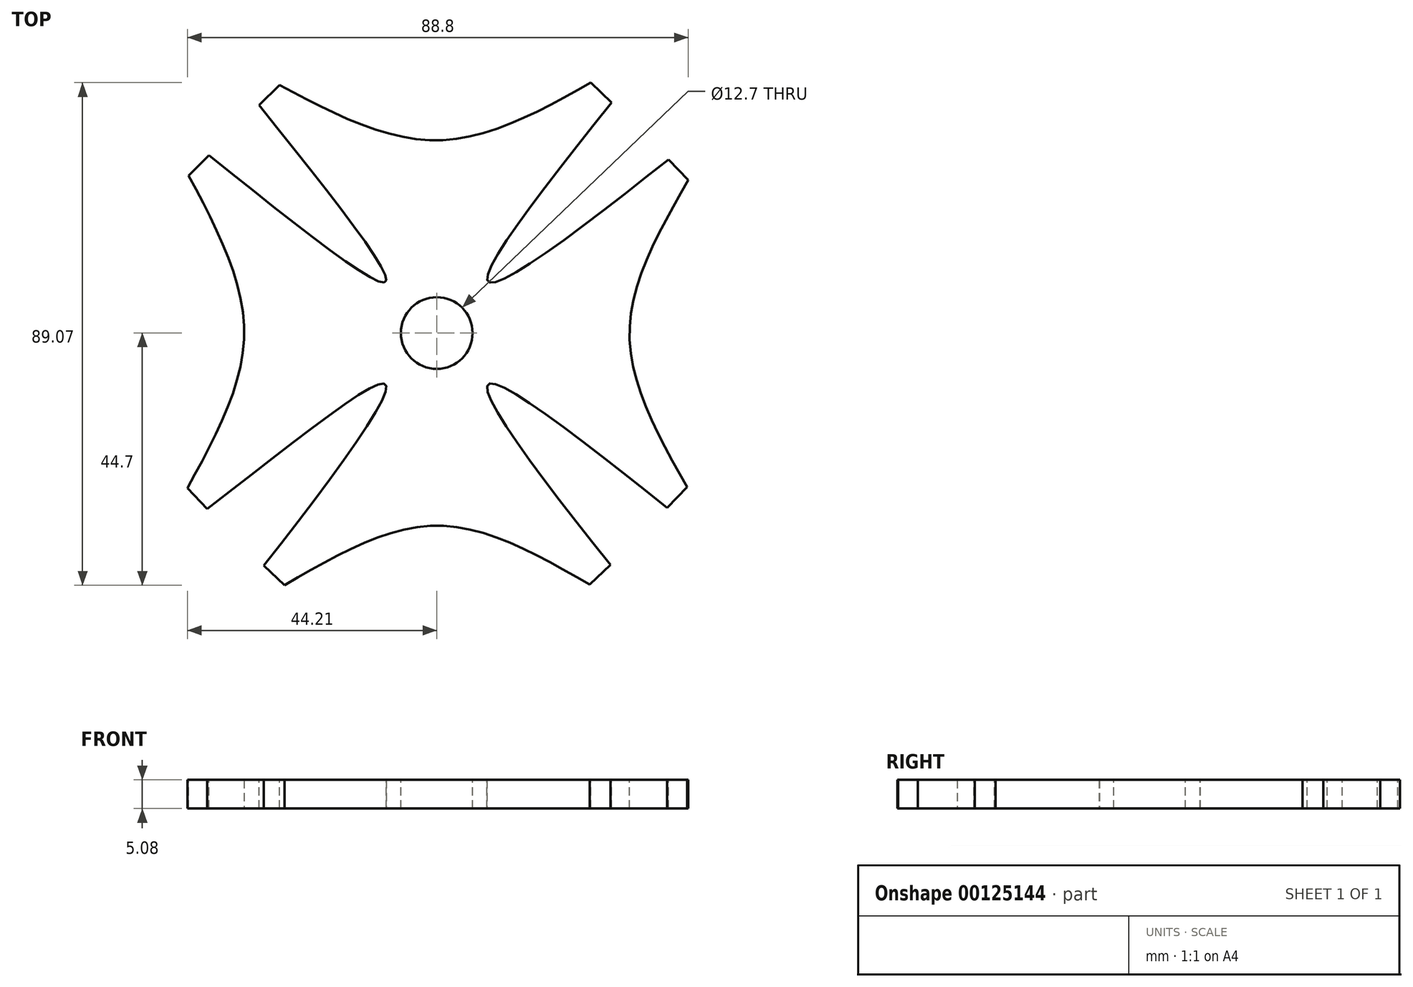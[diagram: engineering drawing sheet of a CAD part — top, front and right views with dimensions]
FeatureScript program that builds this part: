
annotation { "Feature Type Name" : "Feature", "Feature Type Description" : "" }
export const myFeature = defineFeature(function(context is Context, id is Id, definition is map)
    precondition{}
    {
        {
            var Q0;
            Q0=qCreatedBy(makeId("Top.planeOp"),FACE);
            var sketch = newSketch(context, id + "F0", { "sketchPlane" : qUnion([Q0])});
            skCircle(sketch, "E0", {"center": v(0, 0) * mm, "radius": 6.35 * mm});
            skPoint(sketch, "E1", {"position": v(0, -6.35) * mm});
            skPoint(sketch, "E2", {"position": v(6.35, 0) * mm});
            skPoint(sketch, "E3", {"position": v(0, 6.35) * mm});
            skPoint(sketch, "E4", {"position": v(-6.35, 0) * mm});
            skLineSegment(sketch, "E5", {"start": v(0, 6.35) * mm, "end": v(0, 50.8) * mm});
            skLineSegment(sketch, "E6", {"start": v(0, -6.35) * mm, "end": v(0, -50.8) * mm});
            skLineSegment(sketch, "E7", {"start": v(-6.35, 0) * mm, "end": v(-50.8, 0) * mm});
            skLineSegment(sketch, "E8", {"start": v(6.35, 0) * mm, "end": v(50.8, 0) * mm});
            skSolve(sketch);
        }
        {
            var Q0;
            Q0=qCreatedBy(makeId("Top.planeOp"),FACE);
            var sketch = newSketch(context, id + "F1", { "sketchPlane" : qUnion([Q0])});
            skFitSpline(sketch, "E9", {"points": [v(-40.38, 31.49) * mm, v(-9.1, 9.1) * mm, v(-31.49, 40.38) * mm], "startDerivative": vector(89.8, -71.84) * mm, "endDerivative": vector(-71.84, 89.8) * mm});
            skFitSpline(sketch, "E10", {"points": [v(31, 40.86) * mm, v(9.1, 9.1) * mm, v(41.08, 30.77) * mm], "startDerivative": vector(-71.84, -89.8) * mm, "endDerivative": vector(89.8, 71.84) * mm});
            skFitSpline(sketch, "E11", {"points": [v(30.77, -41.08) * mm, v(9.1, -9.1) * mm, v(40.86, -31) * mm], "startDerivative": vector(-71.84, 89.8) * mm, "endDerivative": vector(89.8, -71.84) * mm});
            skLineSegment(sketch, "E12", {"start": v(31, 40.86) * mm, "end": v(27.33, 44.37) * mm});
            skLineSegment(sketch, "E13", {"start": v(41.08, 30.77) * mm, "end": v(44.6, 27.1) * mm});
            skLineSegment(sketch, "E14", {"start": v(40.86, -31) * mm, "end": v(44.37, -27.33) * mm});
            skLineSegment(sketch, "E15", {"start": v(30.77, -41.08) * mm, "end": v(27.1, -44.6) * mm});
            skLineSegment(sketch, "E16", {"start": v(-30.65, -41.19) * mm, "end": v(-26.98, -44.7) * mm});
            skLineSegment(sketch, "E17", {"start": v(-40.69, -31.16) * mm, "end": v(-44.2, -27.5) * mm});
            skLineSegment(sketch, "E18", {"start": v(-40.38, 31.49) * mm, "end": v(-43.97, 27.9) * mm});
            skLineSegment(sketch, "E19", {"start": v(-31.49, 40.38) * mm, "end": v(-27.9, 43.97) * mm});
            skPoint(sketch, "E20", {"position": v(-34.13, 0) * mm});
            skPoint(sketch, "E21", {"position": v(34.17, 0) * mm});
            skFitSpline(sketch, "E22", {"points": [v(-43.97, 27.9) * mm, v(-34.13, 0) * mm, v(-44.2, -27.5) * mm], "startDerivative": vector(29.62, -55.78) * mm, "endDerivative": vector(-30.14, -55) * mm});
            skPoint(sketch, "E23", {"position": v(0, 34.16) * mm});
            skPoint(sketch, "E24", {"position": v(0, -34.14) * mm});
            skFitSpline(sketch, "E25", {"points": [v(-27.9, 43.97) * mm, v(0, 34.16) * mm, v(27.33, 44.37) * mm], "startDerivative": vector(55.8, -29.6) * mm, "endDerivative": vector(54.65, 30.47) * mm});
            skFitSpline(sketch, "E26", {"points": [v(44.6, 27.1) * mm, v(34.17, 0) * mm, v(44.37, -27.33) * mm], "startDerivative": vector(-31.16, -54.18) * mm, "endDerivative": vector(30.7, -54.67) * mm});
            skFitSpline(sketch, "E27", {"points": [v(-26.98, -44.7) * mm, v(0, -34.14) * mm, v(27.1, -44.6) * mm], "startDerivative": vector(53.95, 31.63) * mm, "endDerivative": vector(54.2, -31.4) * mm});
            skFitSpline(sketch, "E28", {"points": [v(-40.69, -31.16) * mm, v(-9.1, -9.1) * mm, v(-30.65, -41.19) * mm], "startDerivative": vector(91.11, 69.9) * mm, "endDerivative": vector(-71.08, -90) * mm});
            skSolve(sketch);
        }
        {
            var Q0;
            Q0=makeQuery(id+"F1.imprint","IMPRINT",FACE,{"disambiguationData":[TD([[makeQuery(id+"F1.imprint","IMPRINT",EDGE,{"derivedFrom":sQuery(id+"F1.wireOp",EDGE,"E9")}),-1.0]])]});
            extrude(context, id + "F2", {"entities" : qUnion([Q0]), "oppositeDirection" : true, "depth" : 5.08 * mm});
        }
        {
            var Q0;
            {var subQ0=sQuery(id+"F0.wireOp",EDGE,"E0");var subQ1=makeQuery(id+"F0.imprint","IMPRINT",VERTEX,{"disambiguationData":[OD(0.0)],"derivedFrom":subQ0});Q0=makeQuery(id+"F0.imprint","IMPRINT",FACE,{"disambiguationData":[TD([[makeQuery(id+"F0.imprint","IMPRINT",EDGE,{"disambiguationData":[TD([[subQ1,1.0]])],"derivedFrom":subQ0}),1.0]])]});}
            var Q1;
            Q1=makeQuery(id+"F2.opExtrude","CAP_FACE",FACE,{"disambiguationData":[OSD([sQuery(id+"F1.wireOp",EDGE,"E9"),sQuery(id+"F1.wireOp",EDGE,"E10"),sQuery(id+"F1.wireOp",EDGE,"E11"),sQuery(id+"F1.wireOp",EDGE,"E12"),sQuery(id+"F1.wireOp",EDGE,"E13"),sQuery(id+"F1.wireOp",EDGE,"E14"),sQuery(id+"F1.wireOp",EDGE,"E15"),sQuery(id+"F1.wireOp",EDGE,"E16"),sQuery(id+"F1.wireOp",EDGE,"E17"),sQuery(id+"F1.wireOp",EDGE,"E18"),sQuery(id+"F1.wireOp",EDGE,"E19"),sQuery(id+"F1.wireOp",EDGE,"E22"),sQuery(id+"F1.wireOp",EDGE,"E25"),sQuery(id+"F1.wireOp",EDGE,"E26"),sQuery(id+"F1.wireOp",EDGE,"E27"),sQuery(id+"F1.wireOp",EDGE,"E28")])],"isStart":false});
            extrude(context, id + "F3", {"entities" : qUnion([Q0]), "operationType" : NewBodyOperationType.REMOVE, "endBound" : BoundingType.UP_TO_SURFACE, "oppositeDirection" : true, "endBoundEntityFace" : qUnion([Q1]), "depth" : 5.08 * mm});
        }
    });
